# Revit family: Clamp_joint_Profile_SX_types_p_r_i_81017
name_source: partatom
category: Generic Models
revit_build: Autodesk Revit 2018 (Build: 20170223_1515(x64)
units: mm (PartAtom-declared; Revit-internal decimal feet)

## family parameters
Always vertical = No
Can host rebar = No
Cut with Voids When Loaded = No
Part Type = Normal
Room Calculation Point = No
Round Connector Dimension = Use Diameter
Shared = No
Work Plane-Based = Yes

## types (18) — shared parameters
Default Elevation = 1219 mm

## per-type parameters (varying)
| type | Model | URL |
| SX Profil 20/35 | Clamp joint SX 20/35 | https://katalog.haucon.no |
| SX Profil 21/35 | Clamp joint SX 21/35 | https://katalog.haucon.no |
| SX Profil 22/35 | Clamp joint SX 22/35 | https://katalog.haucon.no |
| SX Profil 24/35 | Clamp joint SX 24/35 | https://katalog.haucon.no |
| SX Profil 23/35 | Clamp joint SX 23/35 | https://katalog.haucon.no |
| SX Profil 25/35 | Clamp joint SX 25/35 | https://katalog.haucon.no |
| SX Profil 30/45 | Clamp joint SX 30/45 | https://katalog.haucon.no |
| SX Profil 31/45 | Clamp joint SX 31/45 | https://katalog.haucon.no |
| SX Profil 32/45 | Clamp joint SX 32/45 | https://katalog.haucon.no |
| SX Profil 33/45 | Clamp joint SX 33/45 | https://katalog.haucon.no |
| SX Profil 34/45 | Clamp joint SX 34 /45 | hhttps://katalog.haucon.no |
| SX Profil 35/45 | Clamp joint SX 35/45 | https://katalog.haucon.no |
| SX Profil 40/55 | Clamp joint SX 40/55 | https://katalog.haucon.no |
| SX Profil 41/55 | Clamp joint SX 41/55 | https://katalog.haucon.no |
| SX Profil 42/55 | Clamp joint SX 42/55 | http://haucon.ipb.no |
| SX Profil 43/55 | Clamp joint SX 43/55 | https://katalog.haucon.no |
| SX Profil 44/55 | Clamp joint SX 44/55 | https://katalog.haucon.no |
| SX Profil 45/55 | Clamp joint SX 45/55 | https://katalog.haucon.no |

## geometry (parser evidence)
native form markers: Sweep x17
no freeform markers — native parametric forms only
